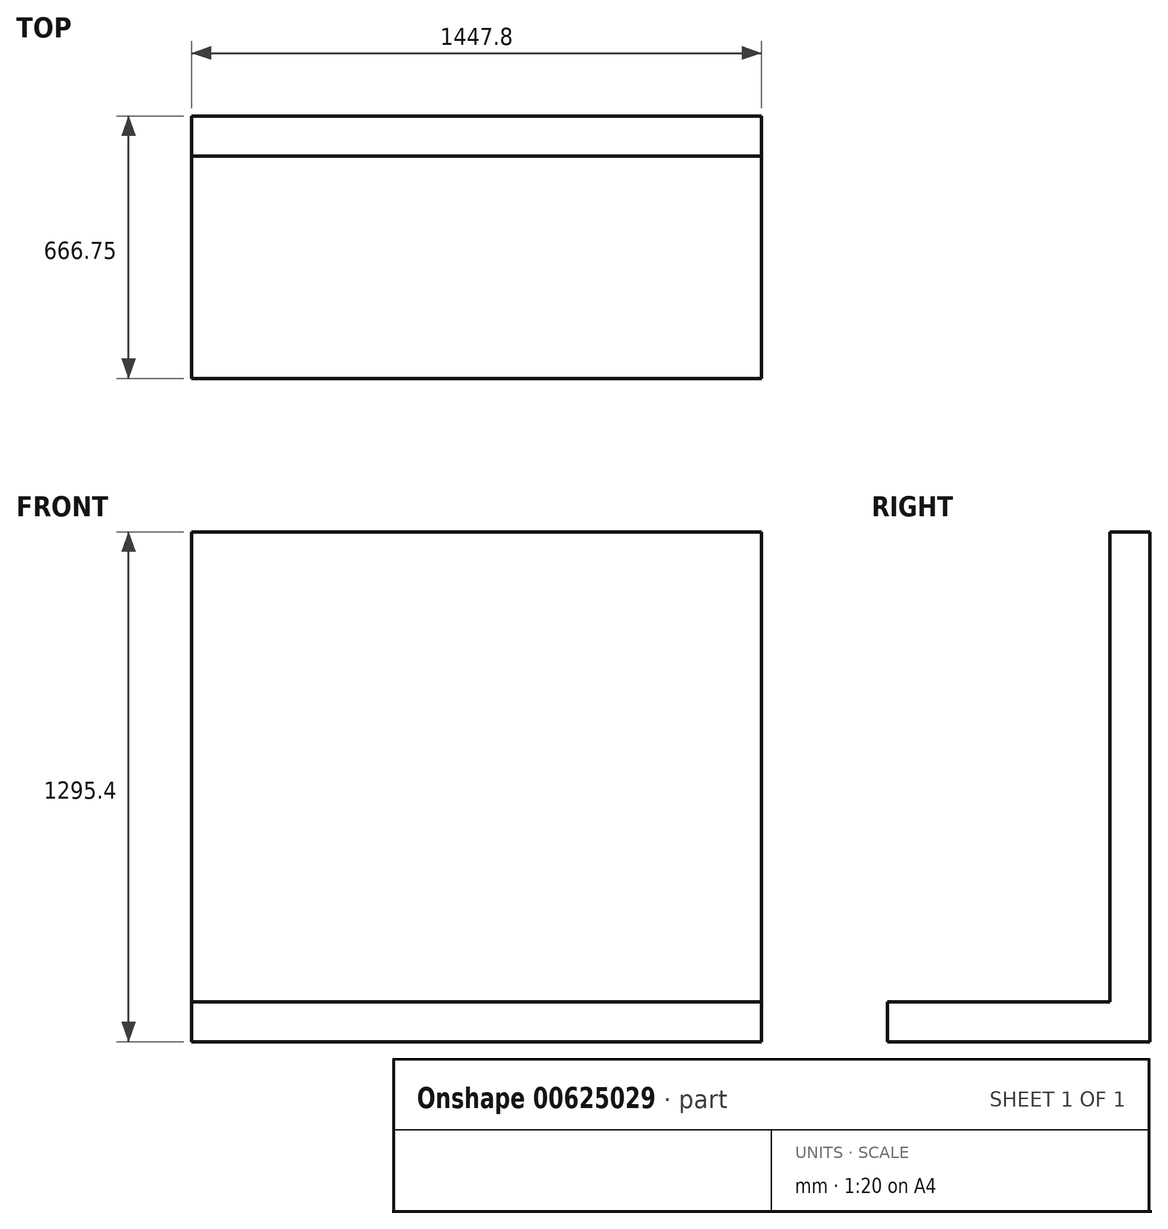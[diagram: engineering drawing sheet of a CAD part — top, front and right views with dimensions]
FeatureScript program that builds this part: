
annotation { "Feature Type Name" : "Feature", "Feature Type Description" : "" }
export const myFeature = defineFeature(function(context is Context, id is Id, definition is map)
    precondition{}
    {
        {
            var Q0;
            Q0=qCreatedBy(makeId("Right.planeOp"),FACE);
            var sketch = newSketch(context, id + "F0", { "sketchPlane" : qUnion([Q0])});
            skLineSegment(sketch, "E0.bottom", {"start": v(-210.98, 28.18) * mm, "end": v(354.17, 28.18) * mm});
            skLineSegment(sketch, "E0.top", {"start": v(-210.98, -73.42) * mm, "end": v(354.17, -73.42) * mm});
            skLineSegment(sketch, "E0.left", {"start": v(-210.98, 28.18) * mm, "end": v(-210.98, -73.42) * mm});
            skLineSegment(sketch, "E0.right", {"start": v(354.17, 28.18) * mm, "end": v(354.17, -73.42) * mm});
            skSolve(sketch);
        }
        {
            var Q0;
            Q0=makeQuery(id+"F0.imprint","IMPRINT",FACE,{"disambiguationData":[TD([[makeQuery(id+"F0.imprint","IMPRINT",EDGE,{"derivedFrom":sQuery(id+"F0.wireOp",EDGE,"E0.bottom")}),-1.0]])]});
            extrude(context, id + "F1", {"entities" : qUnion([Q0]), "depth" : 1447.8 * mm, "offsetDistance" : 25.4 * mm});
        }
        {
            var Q0;
            Q0=qCreatedBy(makeId("Right.planeOp"),FACE);
            var sketch = newSketch(context, id + "F2", { "sketchPlane" : qUnion([Q0])});
            skPoint(sketch, "E1.0", {"position": v(354.17, -73.42) * mm});
            skLineSegment(sketch, "E2.bottom", {"start": v(354.17, -73.42) * mm, "end": v(455.77, -73.42) * mm});
            skLineSegment(sketch, "E2.top", {"start": v(354.17, 1221.98) * mm, "end": v(455.77, 1221.98) * mm});
            skLineSegment(sketch, "E2.left", {"start": v(354.17, -73.42) * mm, "end": v(354.17, 1221.98) * mm});
            skLineSegment(sketch, "E2.right", {"start": v(455.77, -73.42) * mm, "end": v(455.77, 1221.98) * mm});
            skSolve(sketch);
        }
        {
            var Q0;
            Q0=makeQuery(id+"F2.imprint","IMPRINT",FACE,{"disambiguationData":[TD([[makeQuery(id+"F2.imprint","IMPRINT",EDGE,{"derivedFrom":sQuery(id+"F2.wireOp",EDGE,"E2.bottom")}),1.0]])]});
            extrude(context, id + "F3", {"entities" : qUnion([Q0]), "operationType" : NewBodyOperationType.ADD, "depth" : 1447.8 * mm, "offsetDistance" : 25.4 * mm});
        }
    });
